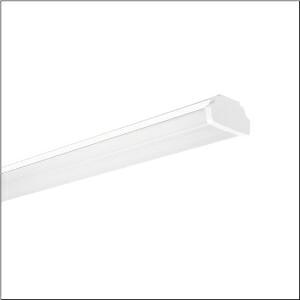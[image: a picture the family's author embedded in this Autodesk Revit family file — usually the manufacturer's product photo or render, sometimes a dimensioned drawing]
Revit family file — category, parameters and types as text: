
# Revit family: modario_r__31_ho_53bm812c1v6105_fe2c
name_source: partatom
category: Lighting Fixtures
units: mm (PartAtom-declared; Revit-internal decimal feet)

## family parameters
Cut with Voids When Loaded = No
Host = Face
Light Source = No
Part Type = Normal
Room Calculation Point = No
Round Connector Dimension = Use Diameter
Shared = No

## types (1)
- --- (1 x LED, 10560 lm, 63.8 W, 6500K)
    Apparent Load = 64 VA
    CIE Flux Codes = 47 80 95 92 100
    Color Rendering = 80
    Color Temperature = 6500K
    Default Elevation = 1800 mm
    Description = Modario® 31 HO, luminaire insert, of sheet steel, coil coated, white, length: 1.495mm, width: 81mm, height: 82mm, 5x system unit, system units: 299mm, LED rated luminous flux: 10.560lm, light colour: 865, control gear: ON/OFF Multilumen, CLOi, control gear: ECG Multilumen, with plug, 3-pole, with phase selection, mains connection: 220..240V, AC, 50/60Hz, start of lifetime: 64W, end of service life: 73W, through-wiring accessed according to module size, primary optical cover: cover, of PMMA, light emission: direct distribution, primary light characteristic: symmetric, protection rating (complete): IP20, protection rating (LED compartment): IP50, insulation class (complete): insulation class I (protective earthing), certification: CE, ENEC, VDE, UKCA, impact resistance: IK03, permissible ambient temperature for indoor applications: -35..+35°C, corresponds to IFS (International Featured Standards) requirements for safety and quality in the food industry, reducing of maximum allowable ambient temperature of 5°C with ceiling mounting, packaging unit: 1 piece
    Height = 92 mm
    Lamp = 1 x LED
    Lamp Light Flux = 10560 lm
    Lamp Power = 63.8 W
    Lamp count = 1
    Length = 1495 mm
    Luminous efficacy = 166 lm/W
    Manufacturer = Siteco
    ModVariant = No
    Model = 53BM812C1V6105
    Mounting Place = Ceiling
    Mounting Type = Pendant
    Number of Poles = 1
    OnlyDefault = Yes
    Power Factor = 1
    Product Name = Modario® 31 HO
    Product group = luminaire insert
    ProductGroupID = 901
    Protection Class = Protection class I
    Protection Degree = IP 20
    RLX_Detail_Level = 1
    RLX_Emergency_Light_Flux = 0 lm
    RLX_Emergency_Type = 0
    RLX_Emergency_Type_DB = No
    RlxData = <blob elided: 40233 chars, md5=ab907c5c>
    Socket = socket
    Standby Power = 0 W
    System Light Flux = 10560 lm
    System Power = 64 W
    Type Comments = factory setting: luminous flux: 100 % | (A | C | E) | 144 mA
    Type Image = l_1300283.jpg
    URL = http://relux.com
    VarID = @adj_138111
    Voltage = 0 V
    Weight = 0.00 kg
    Width = 81 mm

## geometry (parser evidence)
native form markers: Blend x4, Sweep x12
no freeform markers — native parametric forms only
